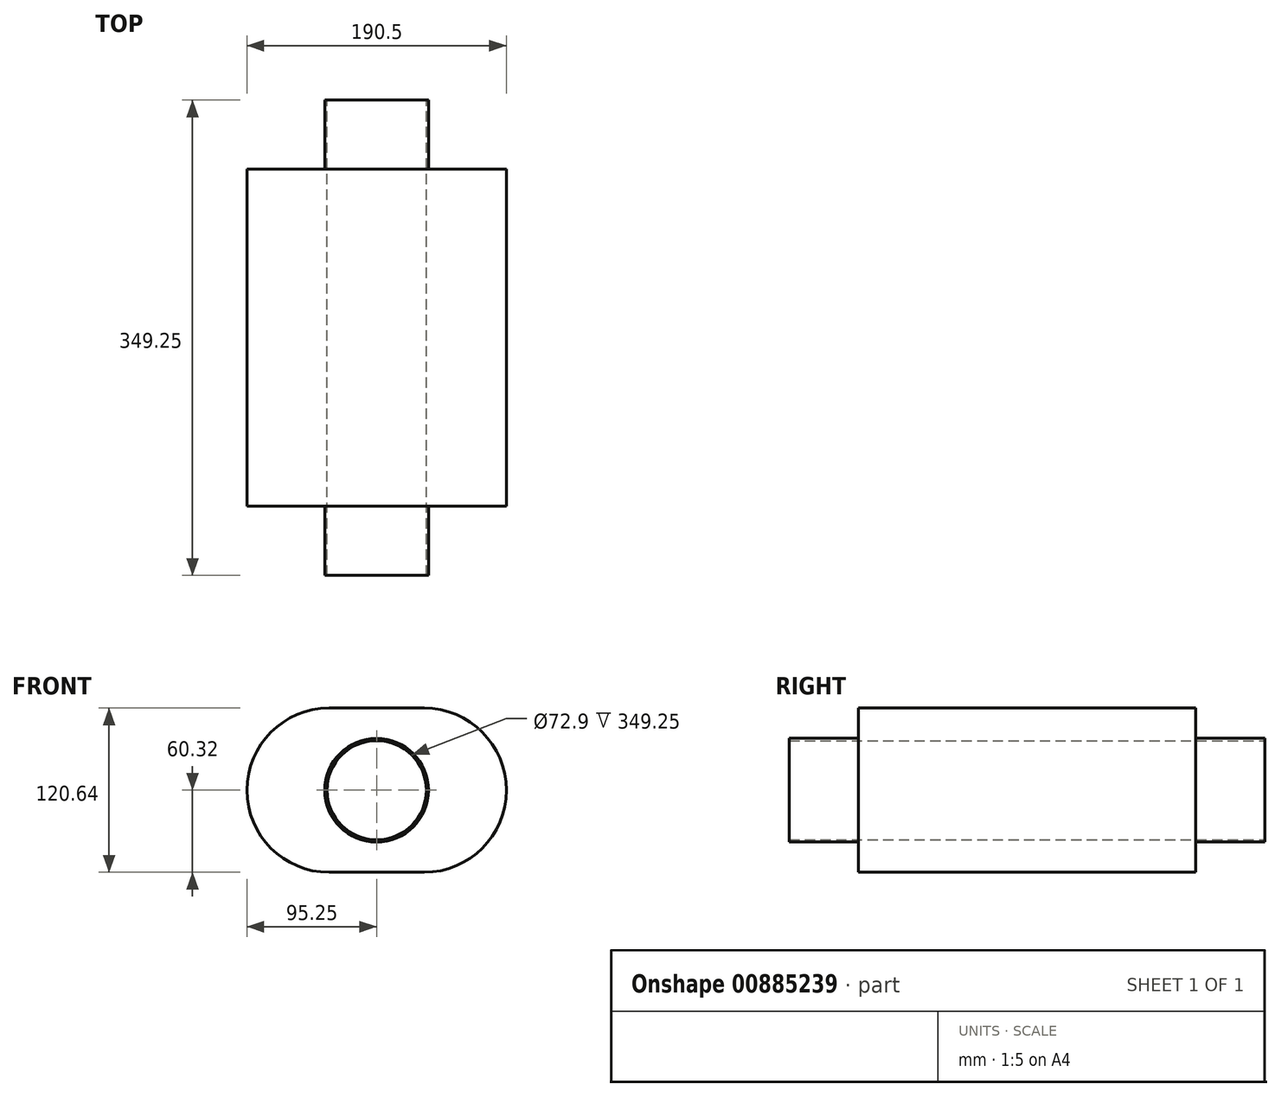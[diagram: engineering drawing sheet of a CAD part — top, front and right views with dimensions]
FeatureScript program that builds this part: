
annotation { "Feature Type Name" : "Feature", "Feature Type Description" : "" }
export const myFeature = defineFeature(function(context is Context, id is Id, definition is map)
    precondition{}
    {
        {
            var Q0;
            Q0=qCreatedBy(makeId("Front.planeOp"),FACE);
            var sketch = newSketch(context, id + "F0", { "sketchPlane" : qUnion([Q0])});
            skArc(sketch, "E0", {"start": v(-34.93, 60.33) * mm, "mid": v(-95.25, 0) * mm, "end": v(-34.93, -60.33) * mm});
            skArc(sketch, "E1.MirrorC", {"start": v(34.93, 60.33) * mm, "mid": v(95.25, 0) * mm, "end": v(34.93, -60.33) * mm});
            skLineSegment(sketch, "E2", {"start": v(-34.93, 60.33) * mm, "end": v(34.93, 60.33) * mm});
            skLineSegment(sketch, "E3.MirrorCS", {"start": v(-34.93, -60.33) * mm, "end": v(34.93, -60.33) * mm});
            skSolve(sketch);
        }
        {
            var Q0;
            Q0=makeQuery(id+"F0.imprint","IMPRINT",FACE,{"disambiguationData":[TD([[makeQuery(id+"F0.imprint","IMPRINT",EDGE,{"derivedFrom":sQuery(id+"F0.wireOp",EDGE,"E0")}),1.0]])]});
            extrude(context, id + "F1", {"entities" : qUnion([Q0]), "depth" : 247.65 * mm, "offsetDistance" : 25.4 * mm});
        }
        {
            var Q0;
            Q0=makeQuery(id+"F1.opExtrude","CAP_FACE",FACE,{"disambiguationData":[OSD([sQuery(id+"F0.wireOp",EDGE,"E0"),sQuery(id+"F0.wireOp",EDGE,"E1.MirrorC"),sQuery(id+"F0.wireOp",EDGE,"E2"),sQuery(id+"F0.wireOp",EDGE,"E3.MirrorCS")])],"isStart":false});
            var sketch = newSketch(context, id + "F2", { "sketchPlane" : qUnion([Q0])});
            skCircle(sketch, "E4", {"center": v(0, 0) * mm, "radius": 38.1 * mm});
            skCircle(sketch, "E5", {"center": v(0, 0) * mm, "radius": 36.45 * mm});
            skSolve(sketch);
        }
        {
            var Q0;
            Q0=makeQuery(id+"F2.imprint","IMPRINT",FACE,{"disambiguationData":[TD([[makeQuery(id+"F2.imprint","IMPRINT",EDGE,{"derivedFrom":sQuery(id+"F2.wireOp",EDGE,"E4")}),1.0]])]});
            extrude(context, id + "F3", {"entities" : qUnion([Q0]), "operationType" : NewBodyOperationType.ADD, "depth" : 50.8 * mm, "offsetDistance" : 25.4 * mm});
        }
        {
            var Q0;
            Q0=makeQuery(id+"F1.opExtrude","CAP_FACE",FACE,{"disambiguationData":[OSD([sQuery(id+"F0.wireOp",EDGE,"E0"),sQuery(id+"F0.wireOp",EDGE,"E1.MirrorC"),sQuery(id+"F0.wireOp",EDGE,"E2"),sQuery(id+"F0.wireOp",EDGE,"E3.MirrorCS")])],"isStart":true});
            var sketch = newSketch(context, id + "F4", { "sketchPlane" : qUnion([Q0])});
            skCircle(sketch, "E6", {"center": v(0, 0) * mm, "radius": 38.1 * mm});
            skCircle(sketch, "E7", {"center": v(0, 0) * mm, "radius": 36.45 * mm});
            skSolve(sketch);
        }
        {
            var Q0;
            Q0=makeQuery(id+"F4.imprint","IMPRINT",FACE,{"disambiguationData":[TD([[makeQuery(id+"F4.imprint","IMPRINT",EDGE,{"derivedFrom":sQuery(id+"F4.wireOp",EDGE,"E6")}),1.0]])]});
            extrude(context, id + "F5", {"entities" : qUnion([Q0]), "operationType" : NewBodyOperationType.ADD, "depth" : 50.8 * mm, "offsetDistance" : 25.4 * mm});
        }
        {
            var Q0;
            Q0=makeQuery(id+"F3.boolean.opBoolean","SPLIT",FACE,{"disambiguationData":[TD([makeQuery(id+"F3.opExtrude","SWEPT_FACE",FACE,{"disambiguationData":[OSD([sQuery(id+"F2.wireOp",EDGE,"E5")])]})])],"derivedFrom":makeQuery(id+"F1.opExtrude","CAP_FACE",FACE,{"disambiguationData":[OSD([sQuery(id+"F0.wireOp",EDGE,"E0"),sQuery(id+"F0.wireOp",EDGE,"E1.MirrorC"),sQuery(id+"F0.wireOp",EDGE,"E2"),sQuery(id+"F0.wireOp",EDGE,"E3.MirrorCS")])],"isStart":false})});
            extrude(context, id + "F6", {"entities" : qUnion([Q0]), "operationType" : NewBodyOperationType.REMOVE, "oppositeDirection" : true, "depth" : 330.2 * mm, "offsetDistance" : 25.4 * mm});
        }
    });
